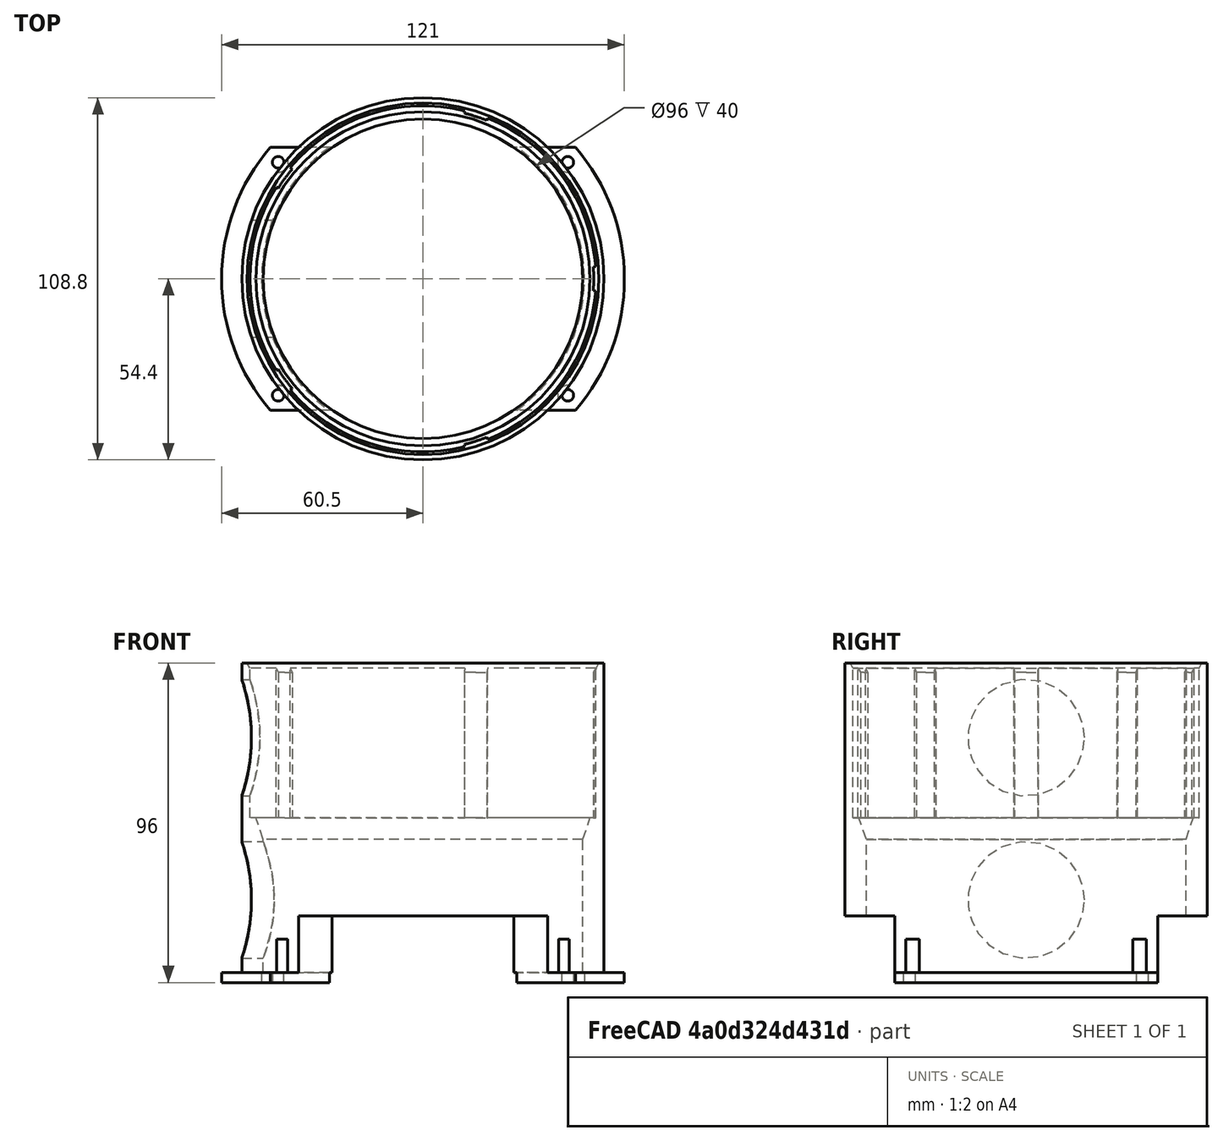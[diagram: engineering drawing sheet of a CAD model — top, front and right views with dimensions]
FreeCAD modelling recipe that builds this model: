
FCSTD DOCUMENT  (FreeCAD 0.19R24291 (Git))
Label: Фланец стаканов3
License: All rights reserved
LicenseURL: http://en.wikipedia.org/wiki/All_rights_reserved
objects: Sketcher::SketchObject×7, PartDesign::Mirrored×4, PartDesign::Pocket×3, PartDesign::Revolution×2, PartDesign::MultiTransform×2, Mesh::Feature×1, PartDesign::Pad×1, PartDesign::PolarPattern×1, PartDesign::Plane×1, PartDesign::Body×1
note: 28 computed .brp shape members not serialized (recipe doc carries the construction recipe); baked Part::Feature solids carry a one-line shape summary decoded from their .brp

FEATURE [Mesh::Feature] ______________________________2  label="СъёмникСтаканов2"
FEATURE [Sketcher::SketchObject] Sketch
  FullyConstrained = true
  MapMode = 5
  Support = -> [XY_Plane]
  sketch-geometry (5):
    g0: ArcOfCircle CenterX=0 CenterY=0 CenterZ=0 NormalX=0 NormalY=0 NormalZ=1 AngleXU=0 Radius=60.5 StartAngle=0 EndAngle=1.5708
    g1: ArcOfCircle CenterX=0 CenterY=0 CenterZ=0 NormalX=0 NormalY=0 NormalZ=1 AngleXU=0 Radius=48.5 StartAngle=0 EndAngle=1.5708
    g2: LineSegment StartX=48.5 StartY=0 StartZ=0 EndX=60.5 EndY=0 EndZ=0
    g3: Circle CenterX=43.5 CenterY=35 CenterZ=0 NormalX=0 NormalY=0 NormalZ=1 AngleXU=0 Radius=1.75
    g4: LineSegment StartX=3.7e-15 StartY=60.5 StartZ=0 EndX=3e-15 EndY=48.5 EndZ=0
  constraints (15):
    c: Coincident(g0,g-1)
    c: PointOnObject(g0,g-1)
    c: Diameter(g0) = 121
    c: Coincident(g1,g0)
    c: PointOnObject(g1,g-1)
    c: Diameter(g1) = 97
    c: Coincident(g2,g1)
    c: Coincident(g2,g0)
    c: Diameter(g3) = 3.5
    c: DistanceX(g3) = 43.5
    c: DistanceY(g3) = 35
    c: PointOnObject(g1,g-2)
    c: PointOnObject(g0,g-2)
    c: Coincident(g4,g0)
    c: Coincident(g4,g1)
FEATURE [Sketcher::SketchObject] Sketch001
  FullyConstrained = true
  MapMode = 5
  Placement = pos=(0,0,0) rot=(1,0,0;1.5708rad)
  Support = -> [XZ_Plane]
  sketch-geometry (8):
    g0: LineSegment StartX=48 StartY=40 StartZ=0 EndX=50.2 EndY=46.5 EndZ=0
    g1: LineSegment StartX=50.2 StartY=46.5 StartZ=0 EndX=52 EndY=46.5 EndZ=0
    g2: LineSegment StartX=52 StartY=46.5 StartZ=0 EndX=52 EndY=91.5 EndZ=0
    g3: LineSegment StartX=52 StartY=91.5 StartZ=0 EndX=52.8 EndY=93.0002 EndZ=0
    g4: LineSegment StartX=52.8 StartY=93.0002 StartZ=0 EndX=54.4 EndY=93.0002 EndZ=0
    g5: LineSegment StartX=54.4 StartY=93.0002 StartZ=0 EndX=54.4 EndY=0 EndZ=0
    g6: LineSegment StartX=54.4 StartY=0 StartZ=0 EndX=48 EndY=0 EndZ=0
    g7: LineSegment StartX=48 StartY=0 StartZ=0 EndX=48 EndY=40 EndZ=0
  constraints (24):
    c: Coincident(g0,g1)
    c: Horizontal(g1)
    c: Coincident(g1,g2)
    c: Vertical(g2)
    c: Coincident(g2,g3)
    c: Coincident(g3,g4)
    c: Horizontal(g4)
    c: Coincident(g4,g5)
    c: Vertical(g5)
    c: Coincident(g5,g6)
    c: Horizontal(g6)
    c: Coincident(g6,g7)
    c: Coincident(g7,g0)
    c: Vertical(g7)
    c: Distance(g0,g-2) = 48
    c: Distance(g0,g-2) = 50.2
    c: Distance(g1,g-2) = 52
    c: Distance(g4) = 1.6
    c: Distance(g7) = 40
    c: Distance(g2) = 45
    c: DistanceY(g0,g0) = 6.5
    c: PointOnObject(g5,g-1)
    c: Distance(g1,g5) = 2.4
    c: Angle(g2,g3) = 2.65168
FEATURE [PartDesign::Revolution] Revolution
  Angle = 360
  Axis = (0,-2e-16,1)
  Base = (0,0,0)
  Placement = pos=(0,0,0) rot=(1,0,0;1.5708rad)
  Profile = -> Sketch001
  ReferenceAxis = -> Sketch001 [V_Axis]
  Reversed = true
FEATURE [PartDesign::Pad] Pad
  BaseFeature = -> Revolution
  Direction = (1,1,1)
  Length = 3
  Length2 = 100
  Placement = pos=(0,0,0) rot=(1,0,0;1.5708rad)
  Profile = -> Sketch
  Reversed = true
  Type = 0
FEATURE [Sketcher::SketchObject] Sketch002
  FullyConstrained = true
  MapMode = 5
  Support = -> [XY_Plane]
  sketch-geometry (1):
    g0: Circle CenterX=43.5 CenterY=35 CenterZ=0 NormalX=0 NormalY=0 NormalZ=1 AngleXU=0 Radius=3
  constraints (3):
    c: Diameter(g0) = 6
    c: DistanceX(g0) = 43.5
    c: DistanceY(g0) = 35
FEATURE [PartDesign::Pocket] Pocket
  BaseFeature = -> Pad
  Length = 10
  Length2 = 100
  Placement = pos=(0,0,0) rot=(1,0,0;1.5708rad)
  Profile = -> Sketch002
  Reversed = true
  Type = 0
FEATURE [Sketcher::SketchObject] Sketch003
  FullyConstrained = true
  MapMode = 5
  Placement = pos=(0,0,0) rot=(1,0,0;1.5708rad)
  Support = -> [XZ_Plane]
  expr: Constraints[23] = Sketch001.Constraints[23]
  expr: Constraints[19] = Sketch001.Constraints[19]
  expr: Constraints[18] = Sketch001.Constraints[18]
  expr: Constraints[20] = Sketch001.Constraints[20]
  expr: Constraints[15] = Sketch001.Constraints[15]
  expr: Constraints[16] = Sketch001.Constraints[16]
  expr: Constraints[14] = Sketch001.Constraints[14]
  expr: Constraints[17] = Sketch001.Constraints[17]
  expr: Constraints[22] = Sketch001.Constraints[22]
  sketch-geometry (12):
    g0: LineSegment StartX=48 StartY=40 StartZ=0 EndX=50.2 EndY=46.5 EndZ=0
    g1: LineSegment StartX=50.2 StartY=46.5 StartZ=0 EndX=52 EndY=46.5 EndZ=0
    g2: LineSegment StartX=52 StartY=46.5 StartZ=0 EndX=52 EndY=91.5 EndZ=0
    g3: LineSegment StartX=52 StartY=91.5 StartZ=0 EndX=52.8 EndY=93.0002 EndZ=0
    g4: LineSegment StartX=52.8 StartY=93.0002 StartZ=0 EndX=54.4 EndY=93.0002 EndZ=0
    g5: LineSegment StartX=54.4 StartY=93.0002 StartZ=0 EndX=54.4 EndY=0 EndZ=0
    g6: LineSegment StartX=54.4 StartY=0 StartZ=0 EndX=48 EndY=0 EndZ=0
    g7: LineSegment StartX=48 StartY=0 StartZ=0 EndX=48 EndY=40 EndZ=0
    g8: LineSegment StartX=52 StartY=91.5 StartZ=0 EndX=51.275 EndY=90.1405 EndZ=0
    g9: LineSegment StartX=51.275 StartY=90.1405 StartZ=0 EndX=51.275 EndY=46.5 EndZ=0
    g10: LineSegment StartX=51.275 StartY=46.5 StartZ=0 EndX=52 EndY=46.5 EndZ=0
    g11: LineSegment StartX=52 StartY=46.5 StartZ=0 EndX=52 EndY=91.5 EndZ=0
  constraints (35):
    c: Coincident(g0,g1)
    c: Horizontal(g1)
    c: Coincident(g1,g2)
    c: Vertical(g2)
    c: Coincident(g2,g3)
    c: Coincident(g3,g4)
    c: Horizontal(g4)
    c: Coincident(g4,g5)
    c: Vertical(g5)
    c: Coincident(g5,g6)
    c: Horizontal(g6)
    c: Coincident(g6,g7)
    c: Coincident(g7,g0)
    c: Vertical(g7)
    c: Distance(g0,g-2) = 48
    c: Distance(g0,g-2) = 50.2
    c: Distance(g1,g-2) = 52
    c: Distance(g4) = 1.6
    c: Distance(g7) = 40
    c: Distance(g2) = 45
    c: DistanceY(g0,g0) = 6.5
    c: PointOnObject(g5,g-1)
    c: Distance(g1,g5) = 2.4
    c: Angle(g2,g3) = 2.65168
    c: Coincident(g8,g9)
    c: Coincident(g9,g10)
    c: Coincident(g10,g11)
    c: Coincident(g11,g8)
    c: Horizontal(g10)
    c: Vertical(g9)
    c: Vertical(g11)
    c: Coincident(g8,g2)
    c: PointOnObject(g9,g1)
    c: Distance(g10) = 0.725
    c: Parallel(g3,g8)
FEATURE [PartDesign::Revolution] Revolution001
  Angle = 4
  Axis = (0,-2e-16,1)
  Base = (0,0,0)
  BaseFeature = -> Pocket
  Placement = pos=(0,0,0) rot=(1,0,0;1.5708rad)
  Profile = -> Sketch003
  ReferenceAxis = -> Sketch003 [V_Axis]
FEATURE [PartDesign::Mirrored] Mirrored
  MirrorPlane = -> Sketch [V_Axis]
  Placement = pos=(0,0,0) rot=(1,0,0;1.5708rad)
FEATURE [PartDesign::Mirrored] Mirrored001
  MirrorPlane = -> Sketch [H_Axis]
  Placement = pos=(0,0,0) rot=(1,0,0;1.5708rad)
FEATURE [PartDesign::MultiTransform] MultiTransform
  BaseFeature = -> Revolution001
  Originals = -> [Pad,Pocket]
  Placement = pos=(0,0,0) rot=(1,0,0;1.5708rad)
  Transformations = -> [Mirrored,Mirrored001]
FEATURE [PartDesign::Mirrored] Mirrored002
  MirrorPlane = -> XZ_Plane
  Placement = pos=(0,0,0) rot=(1,0,0;1.5708rad)
FEATURE [PartDesign::PolarPattern] PolarPattern
  Angle = 360
  Axis = -> Sketch003 [V_Axis]
  Occurrences = 5
  Placement = pos=(0,0,0) rot=(1,0,0;1.5708rad)
FEATURE [PartDesign::MultiTransform] MultiTransform001
  BaseFeature = -> MultiTransform
  Originals = -> [Revolution001]
  Placement = pos=(0,0,0) rot=(1,0,0;1.5708rad)
  Transformations = -> [Mirrored002,PolarPattern]
FEATURE [PartDesign::Plane] DatumPlane
  AttachmentOffset = pos=(0,0,0) rot=(0,1,0;1.5708rad)
  Length = 197.297
  MapMode = 7
  Placement = pos=(-43.9662,32.0364,7.1e-15) rot=(0.811787,0.412918,0.412918;1.77782rad)
  ResizeMode = 0
  Support = -> [MultiTransform001]
  Width = 146.248
FEATURE [Sketcher::SketchObject] Sketch004
  FullyConstrained = false
  MapMode = 5
  Placement = pos=(-43.9662,32.0364,7.1e-15) rot=(0.811787,0.412918,0.412918;1.77782rad)
  Support = -> [DatumPlane]
  sketch-geometry (5):
    g0: LineSegment StartX=0 StartY=0 StartZ=0 EndX=0 EndY=10 EndZ=0
    g1: LineSegment StartX=0 StartY=0 StartZ=0 EndX=0 EndY=-10 EndZ=0
    g2: LineSegment StartX=0 StartY=10 StartZ=0 EndX=13.8862 EndY=10 EndZ=0
    g3: LineSegment StartX=0 StartY=-10 StartZ=0 EndX=13.8862 EndY=-10 EndZ=0
    g4: ArcOfCircle CenterX=13.8862 CenterY=0 CenterZ=0 NormalX=0 NormalY=0 NormalZ=1 AngleXU=0 Radius=10 StartAngle=4.71239 EndAngle=7.85399
  constraints (14):
    c: Coincident(g0,g-1)
    c: PointOnObject(g0,g-2)
    c: Coincident(g1,g0)
    c: PointOnObject(g1,g-2)
    c: Coincident(g2,g0)
    c: Coincident(g3,g1)
    c: Horizontal(g3)
    c: PointOnObject(g4,g-1)
    c: Coincident(g4,g2)
    c: Coincident(g4,g3)
    c: Tangent(g3,g4)
    c: Tangent(g2,g4)
    c: Diameter(g4) = 20
    c: Horizontal(g2)
FEATURE [Sketcher::SketchObject] Sketch005
  FullyConstrained = false
  MapMode = 5
  Placement = pos=(0,0,0) rot=(0.57735,0.57735,0.57735;2.0944rad)
  Support = -> [YZ_Plane]
  sketch-geometry (4):
    g0: LineSegment StartX=39.5 StartY=-3 StartZ=0 EndX=61.2028 EndY=-3 EndZ=0
    g1: LineSegment StartX=61.2028 StartY=-3 StartZ=0 EndX=61.2028 EndY=17 EndZ=0
    g2: LineSegment StartX=61.2028 StartY=17 StartZ=0 EndX=39.5 EndY=17 EndZ=0
    g3: LineSegment StartX=39.5 StartY=17 StartZ=0 EndX=39.5 EndY=-3 EndZ=0
  constraints (11):
    c: Coincident(g0,g1)
    c: Coincident(g1,g2)
    c: Coincident(g2,g3)
    c: Coincident(g3,g0)
    c: Horizontal(g0)
    c: Horizontal(g2)
    c: Vertical(g1)
    c: Vertical(g3)
    c: Distance(g0,g-1) = 3
    c: Distance(g0,g-2) = 39.5
    c: Distance(g1) = 20
FEATURE [PartDesign::Pocket] Pocket002
  BaseFeature = -> MultiTransform001
  Length = 5
  Length2 = 100
  Midplane = true
  Placement = pos=(0,0,0) rot=(1,0,0;1.5708rad)
  Profile = -> Sketch005
  Type = 1
FEATURE [PartDesign::Mirrored] Mirrored003
  BaseFeature = -> Pocket002
  MirrorPlane = -> Sketch005 [V_Axis]
  Originals = -> [Pocket002]
  Placement = pos=(0,0,0) rot=(1,0,0;1.5708rad)
FEATURE [Sketcher::SketchObject] Sketch006
  FullyConstrained = false
  MapMode = 5
  Placement = pos=(0,0,0) rot=(0.57735,0.57735,0.57735;2.0944rad)
  Support = -> [YZ_Plane]
  sketch-geometry (2):
    g0: Circle CenterX=0 CenterY=21.836 CenterZ=0 NormalX=0 NormalY=0 NormalZ=1 AngleXU=0 Radius=17.5
    g1: Circle CenterX=0 CenterY=70.5488 CenterZ=0 NormalX=0 NormalY=0 NormalZ=1 AngleXU=0 Radius=17.5
  constraints (4):
    c: PointOnObject(g0,g-2)
    c: PointOnObject(g1,g-2)
    c: Diameter(g0) = 35
    c: Diameter(g1) = 35
FEATURE [PartDesign::Pocket] Pocket003
  BaseFeature = -> Mirrored003
  Length = 5
  Length2 = 100
  Placement = pos=(0,0,0) rot=(1,0,0;1.5708rad)
  Profile = -> Sketch006
  Type = 1
FEATURE [PartDesign::Body] Body
  Group = -> [Sketch,Sketch001,Revolution,Pad,Sketch002,Pocket,Sketch003,Revolution001,MultiTransform,Mirrored,Mirrored001,MultiTransform001,Mirrored002,PolarPattern,DatumPlane,Sketch004,Sketch005,Pocket002,Mirrored003,Sketch006,Pocket003]
  Origin = -> Origin
  Placement = pos=(0,0,3) rot=(0,0,1;0rad)
  Tip = -> Pocket003
